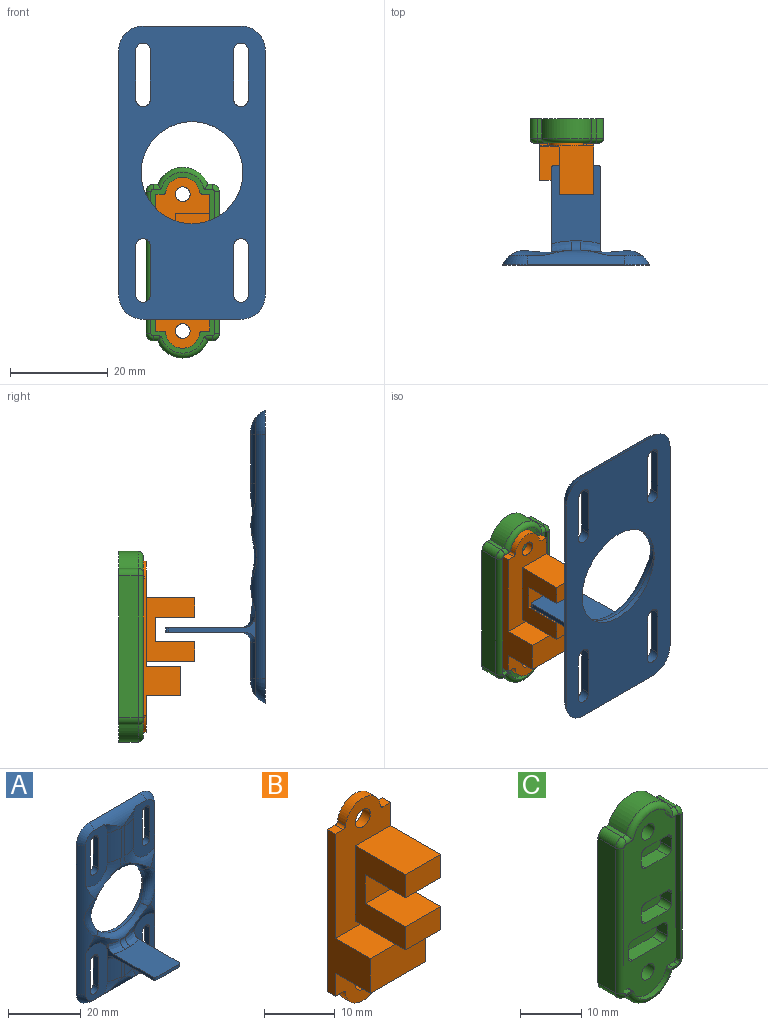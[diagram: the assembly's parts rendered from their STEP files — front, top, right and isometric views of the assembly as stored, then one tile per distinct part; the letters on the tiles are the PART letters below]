
ASSEMBLY  parts=3 mates=2
PART A: 62 faces, bbox 33.1x21.1x63.1 mm
  f0: plane 7.92x1.3mm, normal (0,-1,0), area 10.2mm2, adj f20,f42,f43,f44,f45,f58
  f1: plane 13.04x2.03mm, normal (0,-1,0), area 17.3mm2, adj f23,f36,f46,f47,f48,f49,f50,f51
  f2: cylinder r=1.5mm len=3mm, axis (0,1,0), area 9.4mm2, adj f3,f14,f27,f29
  f3: plane 10x2mm, normal (-1,0,0), area 20mm2, adj f2,f4,f27,f29
  f4: cylinder r=1.5mm len=3mm, axis (0,1,0), area 9.4mm2, adj f3,f14,f27,f29
  f5: cylinder r=1.5mm len=3mm, axis (0,1,0), area 9.4mm2, adj f6,f15,f27,f32
  f6: plane 10x2mm, normal (-1,0,0), area 20mm2, adj f5,f7,f27,f32
  f7: cylinder r=1.5mm len=3mm, axis (0,1,0), area 9.4mm2, adj f6,f15,f27,f32
  f8: cylinder r=1.5mm len=3mm, axis (0,1,0), area 9.4mm2, adj f9,f16,f27,f31
  f9: plane 10x2mm, normal (-1,0,0), area 20mm2, adj f8,f10,f27,f31
  f10: cylinder r=1.5mm len=3mm, axis (0,1,0), area 9.4mm2, adj f9,f16,f27,f31
  f11: cylinder r=1.5mm len=3mm, axis (0,1,0), area 9.4mm2, adj f12,f17,f27,f28
  f12: plane 10x2mm, normal (-1,0,0), area 20mm2, adj f11,f13,f27,f28
  f13: cylinder r=1.5mm len=3mm, axis (0,1,0), area 9.4mm2, adj f12,f17,f27,f28
  f14: plane 10x2mm, normal (1,0,0), area 20mm2, adj f2,f4,f27,f29
  f15: plane 10x2mm, normal (1,0,0), area 20mm2, adj f5,f7,f27,f32
  f16: plane 10x2mm, normal (1,0,0), area 20mm2, adj f8,f10,f27,f31
  f17: plane 10x2mm, normal (1,0,0), area 20mm2, adj f11,f13,f27,f28
  f18: torus R=0.42mm, axis (0,1,0), area 17.4mm2, adj f19,f20,f27,f32
  f19: cylinder r=5mm len=50mm, axis (0,0,-1), area 151.3mm2, adj f18,f21,f27,f31,f32,f35,f46,f53
  f20: cylinder r=5mm len=20mm, axis (-1,0,0), area 74.1mm2, adj f0,f18,f22,f27,f29,f32,f43,f45
  f21: torus R=0.42mm, axis (0,1,0), area 17.4mm2, adj f19,f23,f27,f31
  f22: torus R=0.42mm, axis (0,1,0), area 17.4mm2, adj f20,f24,f27,f29
  f23: cylinder r=5mm len=20mm, axis (-1,0,0), area 74.1mm2, adj f1,f21,f25,f27,f28,f31,f48,f51
  f24: cylinder r=5mm len=50mm, axis (0,0,-1), area 151.3mm2, adj f22,f25,f27,f28,f29,f38,f49,f52
  f25: torus R=0.42mm, axis (0,1,0), area 17.4mm2, adj f23,f24,f27,f28
  f26: plane 2.03x0.12mm, normal (0,-1,0), area 0.2mm2, adj f37,f52,f53,f55
  f27: plane 60x30mm, normal (0,1,0), area 1289.3mm2, adj f2,f3,f4,f5,f6,f7,f8,f9
  f28: plane 18.42x8.42mm, normal (0,-1,0), area 107.2mm2, adj f11,f12,f13,f17,f23,f24,f25,f49
  f29: plane 18.42x8.42mm, normal (0,-1,0), area 107.2mm2, adj f2,f3,f4,f14,f20,f22,f24,f30
  f30: plane 18.22x5.68mm, normal (-1,0,0), area 20.1mm2, adj f29,f39,f40,f52,f54,f57,f61
  f31: plane 18.42x8.42mm, normal (0,-1,0), area 107.2mm2, adj f8,f9,f10,f16,f19,f21,f23,f46
  f32: plane 18.42x8.42mm, normal (0,-1,0), area 107.2mm2, adj f5,f6,f7,f15,f18,f19,f20,f33
  f33: plane 18.22x5.68mm, normal (1,0,0), area 20.1mm2, adj f32,f39,f40,f53,f56,f59,f60
  f34: cylinder r=10.42mm len=20.84mm, axis (0,-1,0), area 56.1mm2, adj f27,f35,f36,f37,f38
  f35: bspline ~14.5x5.46mm, area 53.4mm2, adj f19,f34,f36,f37,f46,f53
  f36: torus R=12.42mm, axis (0,-1,0), area 51.2mm2, adj f1,f34,f35,f38,f46,f49
  f37: torus R=12.42mm, axis (0,-1,0), area 51.2mm2, adj f26,f34,f35,f38,f52,f53
  f38: bspline ~14.5x5.46mm, area 53.4mm2, adj f24,f34,f36,f37,f49,f52
  f39: plane 16.22x10mm, normal (0,0,-1), area 156.2mm2, adj f30,f33,f41,f57,f58,f59,f60,f61
  f40: plane 16.01x10mm, normal (0,0,1), area 155.5mm2, adj f30,f33,f41,f54,f55,f56,f60,f61
  f41: plane 9x1mm, normal (0,-1,0), area 9mm2, adj f39,f40,f60,f61
  f42: cylinder r=10mm len=7.5mm, axis (0,0,1), area 33.8mm2, adj f0,f29,f43,f57
  f43: torus R=9.36mm, axis (0,-1,0), area 9.2mm2, adj f0,f20,f29,f42
  f44: cylinder r=10mm len=7.5mm, axis (0,0,1), area 33.8mm2, adj f0,f32,f45,f59
  f45: torus R=9.36mm, axis (0,-1,0), area 9.2mm2, adj f0,f20,f32,f44
  f46: torus R=9.36mm, axis (0,-1,0), area 38.1mm2, adj f1,f19,f31,f35,f36,f47
  f47: cylinder r=10mm len=10mm, axis (0,0,1), area 45.1mm2, adj f1,f31,f46,f48
  f48: torus R=9.36mm, axis (0,-1,0), area 9.2mm2, adj f1,f23,f31,f47
  f49: torus R=9.36mm, axis (0,-1,0), area 38.1mm2, adj f1,f24,f28,f36,f38,f50
  f50: cylinder r=10mm len=10mm, axis (0,0,1), area 45.1mm2, adj f1,f28,f49,f51
  f51: torus R=9.36mm, axis (0,-1,0), area 9.2mm2, adj f1,f23,f28,f50
  f52: torus R=9.36mm, axis (0,-1,0), area 26.5mm2, adj f24,f26,f29,f30,f37,f38,f54
  f53: torus R=9.36mm, axis (0,-1,0), area 26.5mm2, adj f19,f26,f32,f33,f35,f37,f56
  f54: bspline ~5.71x3.34mm, area 13.1mm2, adj f30,f40,f52,f55
  f55: cylinder r=2mm len=2mm, axis (-1,0,0), area 6.2mm2, adj f26,f40,f54,f56
  f56: bspline ~5.71x3.34mm, area 13.1mm2, adj f33,f40,f53,f55
  f57: torus R=12mm, axis (0,0,-1), area 13.8mm2, adj f30,f39,f42,f58
  f58: cylinder r=2mm len=2mm, axis (1,0,0), area 4mm2, adj f0,f39,f57,f59
  f59: torus R=12mm, axis (0,0,-1), area 13.8mm2, adj f33,f39,f44,f58
  f60: cylinder r=0.5mm len=1mm, axis (0,0,1), area 0.8mm2, adj f33,f39,f40,f41
  f61: cylinder r=0.5mm len=1mm, axis (0,0,-1), area 0.8mm2, adj f30,f39,f40,f41
PART B: 28 faces, bbox 11x11.6x35 mm
  f0: plane 7x4mm, normal (0,-1,0), area 28mm2, adj f1,f22,f23,f26
  f1: plane 28x11.6mm, normal (1,0,0), area 176.8mm2, adj f0,f2,f3,f13,f14,f15,f18,f19
  f2: plane 21.5x11mm, normal (0,-1,0), area 119.3mm2, adj f1,f4,f5,f6,f7,f8,f14,f17
  f3: plane 11x7.5mm, normal (0,-1,0), area 56.3mm2, adj f1,f8,f9,f10,f11,f12,f13,f16
  f4: cylinder r=0.5mm len=1.6mm, axis (0,1,0), area 1.2mm2, adj f2,f5,f14,f15
  f5: cylinder r=3.5mm len=6.95mm, axis (0,1,0), area 16.2mm2, adj f2,f4,f6,f15
  f6: cylinder r=0.5mm len=1.6mm, axis (0,1,0), area 1.2mm2, adj f2,f5,f7,f15
  f7: plane 1.6x1.53mm, normal (0,0,1), area 2.5mm2, adj f2,f6,f8,f15
  f8: plane 28x8.6mm, normal (-1,0,0), area 86.8mm2, adj f2,f3,f7,f9,f15,f18,f19,f20
  f9: plane 1.6x1.53mm, normal (0,0,-1), area 2.5mm2, adj f3,f8,f10,f15
  f10: cylinder r=0.5mm len=1.6mm, axis (0,1,0), area 1.2mm2, adj f3,f9,f11,f15
  f11: cylinder r=3.5mm len=6.95mm, axis (0,1,0), area 16.2mm2, adj f3,f10,f12,f15
  f12: cylinder r=0.5mm len=1.6mm, axis (0,1,0), area 1.2mm2, adj f3,f11,f13,f15
  f13: plane 1.6x1.53mm, normal (0,0,-1), area 2.5mm2, adj f1,f3,f12,f15
  f14: plane 1.6x1.53mm, normal (0,0,1), area 2.5mm2, adj f1,f2,f4,f15
  f15: plane 35x11mm, normal (0,1,0), area 332.5mm2, adj f1,f4,f5,f6,f7,f8,f9,f10
  f16: cylinder r=1.5mm len=3mm, axis (0,1,0), area 15.1mm2, adj f3,f15
  f17: cylinder r=1.5mm len=3mm, axis (0,1,0), area 15.1mm2, adj f2,f15
  f18: plane 11x7mm, normal (0,0,1), area 77mm2, adj f1,f2,f8,f20
  f19: plane 11x7mm, normal (0,0,-1), area 77mm2, adj f1,f3,f8,f20
  f20: plane 11x6mm, normal (0,-1,0), area 66mm2, adj f1,f8,f18,f19
  f21: plane 10x7mm, normal (0,0,1), area 70mm2, adj f1,f2,f22,f24
  f22: plane 13x10mm, normal (-1,0,0), area 90mm2, adj f0,f2,f21,f23,f24,f25,f26,f27
  f23: plane 10x7mm, normal (0,0,-1), area 70mm2, adj f0,f1,f2,f22
  f24: plane 7x4mm, normal (0,-1,0), area 28mm2, adj f1,f21,f22,f25
  f25: plane 8x7mm, normal (0,0,-1), area 56mm2, adj f1,f22,f24,f27
  f26: plane 8x7mm, normal (0,0,1), area 56mm2, adj f0,f1,f22,f27
  f27: plane 7x5mm, normal (0,-1,0), area 35mm2, adj f1,f22,f25,f26
PART C: 71 faces, bbox 15x5x39.9 mm
  f0: plane 37x13mm, normal (0,-1,0), area 332.1mm2, adj f2,f3,f4,f5,f6,f7,f8,f9
  f1: plane 39x15mm, normal (0,1,0), area 516mm2, adj f10,f11,f12,f13,f14,f15,f16,f17
  f2: plane 29x1mm, normal (-1,0,0), area 29mm2, adj f0,f4,f5,f34
  f3: plane 29x1mm, normal (1,0,0), area 29mm2, adj f0,f7,f8,f37
  f4: cylinder r=0.5mm len=1mm, axis (0,1,0), area 0.8mm2, adj f0,f2,f28,f36
  f5: cylinder r=0.5mm len=1mm, axis (0,1,0), area 0.8mm2, adj f0,f2,f21,f32
  f6: cylinder r=4.5mm len=8.59mm, axis (0,1,0), area 11.4mm2, adj f0,f22,f23,f31
  f7: cylinder r=0.5mm len=1mm, axis (0,1,0), area 0.8mm2, adj f0,f3,f24,f35
  f8: cylinder r=0.5mm len=1mm, axis (0,1,0), area 0.8mm2, adj f0,f3,f25,f39
  f9: cylinder r=4.5mm len=8.59mm, axis (0,1,0), area 11.4mm2, adj f0,f26,f27,f40
  f10: cylinder r=5.5mm len=10.25mm, axis (0,1,0), area 52.7mm2, adj f1,f11,f29,f31
  f11: plane 4x0.88mm, normal (0,0,-1), area 3.5mm2, adj f1,f10,f12,f30
  f12: cylinder r=1.5mm len=4mm, axis (0,1,0), area 9.4mm2, adj f1,f11,f13,f32
  f13: plane 29x4mm, normal (1,0,0), area 116mm2, adj f1,f12,f14,f34
  f14: cylinder r=1.5mm len=4mm, axis (0,1,0), area 9.4mm2, adj f1,f13,f15,f36
  f15: plane 4x0.88mm, normal (0,0,1), area 3.5mm2, adj f1,f14,f16,f38
  f16: cylinder r=5.5mm len=10.25mm, axis (0,1,0), area 52.7mm2, adj f1,f15,f17,f40
  f17: plane 4x0.88mm, normal (0,0,1), area 3.5mm2, adj f1,f16,f18,f41
  f18: cylinder r=1.5mm len=4mm, axis (0,1,0), area 9.4mm2, adj f1,f17,f19,f39
  f19: plane 29x4mm, normal (-1,0,0), area 116mm2, adj f1,f18,f20,f37
  f20: cylinder r=1.5mm len=4mm, axis (0,1,0), area 9.4mm2, adj f1,f19,f29,f35
  f21: plane 1.23x1mm, normal (0,0,1), area 1.2mm2, adj f0,f5,f22,f30
  f22: cylinder r=0.5mm len=1mm, axis (0,1,0), area 0.6mm2, adj f0,f6,f21,f30,f31
  f23: cylinder r=0.5mm len=1mm, axis (0,1,0), area 0.6mm2, adj f0,f6,f24,f31,f33
  f24: plane 1.23x1mm, normal (0,0,1), area 1.2mm2, adj f0,f7,f23,f33
  f25: plane 1.23x1mm, normal (0,0,-1), area 1.2mm2, adj f0,f8,f26,f41
  f26: cylinder r=0.5mm len=1mm, axis (0,1,0), area 0.6mm2, adj f0,f9,f25,f40,f41
  f27: cylinder r=0.5mm len=1mm, axis (0,1,0), area 0.6mm2, adj f0,f9,f28,f38,f40
  f28: plane 1.23x1mm, normal (0,0,-1), area 1.2mm2, adj f0,f4,f27,f38
  f29: plane 4x0.88mm, normal (0,0,-1), area 3.5mm2, adj f1,f10,f20,f33
  f30: cylinder r=1mm len=1.53mm, axis (-1,0,0), area 1.8mm2, adj f11,f21,f22,f31,f32
  f31: torus R=4.5mm, axis (0,-1,0), area 20.1mm2, adj f6,f10,f22,f23,f30,f33
  f32: torus R=0.5mm, axis (0,-1,0), area 2.8mm2, adj f5,f12,f30,f34
  f33: cylinder r=1mm len=1.53mm, axis (-1,0,0), area 1.8mm2, adj f23,f24,f29,f31,f35
  f34: cylinder r=1mm len=29mm, axis (0,0,-1), area 45.6mm2, adj f2,f13,f32,f36
  f35: torus R=0.5mm, axis (0,-1,0), area 2.8mm2, adj f7,f20,f33,f37
  f36: torus R=0.5mm, axis (0,-1,0), area 2.8mm2, adj f4,f14,f34,f38
  f37: cylinder r=1mm len=29mm, axis (0,0,1), area 45.6mm2, adj f3,f19,f35,f39
  f38: cylinder r=1mm len=1.53mm, axis (1,0,0), area 1.8mm2, adj f15,f27,f28,f36,f40
  f39: torus R=0.5mm, axis (0,-1,0), area 2.8mm2, adj f8,f18,f37,f41
  f40: torus R=4.5mm, axis (0,-1,0), area 20.1mm2, adj f9,f16,f26,f27,f38,f41
  f41: cylinder r=1mm len=1.53mm, axis (1,0,0), area 1.8mm2, adj f17,f25,f26,f39,f40
  f42: cylinder r=1.5mm len=4mm, axis (0,1,0), area 37.7mm2, adj f0,f1
  f43: cylinder r=1.5mm len=4mm, axis (0,1,0), area 37.7mm2, adj f0,f1
  f44: plane 5x2.5mm, normal (0,0,1), area 12.5mm2, adj f0,f45,f51,f52
  f45: cylinder r=1mm len=2.5mm, axis (0,-1,0), area 3.9mm2, adj f0,f44,f46,f52
  f46: plane 2.5x2mm, normal (-1,0,0), area 5mm2, adj f0,f45,f47,f52
  f47: cylinder r=1mm len=2.5mm, axis (0,-1,0), area 3.9mm2, adj f0,f46,f48,f52
  f48: plane 5x2.5mm, normal (0,0,-1), area 12.5mm2, adj f0,f47,f49,f52
  f49: cylinder r=1mm len=2.5mm, axis (0,-1,0), area 3.9mm2, adj f0,f48,f50,f52
  f50: plane 2.5x2mm, normal (1,0,0), area 5mm2, adj f0,f49,f51,f52
  f51: cylinder r=1mm len=2.5mm, axis (0,-1,0), area 3.9mm2, adj f0,f44,f50,f52
  f52: plane 7x4mm, normal (0,-1,0), area 27.1mm2, adj f44,f45,f46,f47,f48,f49,f50,f51
  f53: plane 5x2.5mm, normal (0,0,1), area 12.5mm2, adj f0,f54,f60,f61
  f54: cylinder r=1mm len=2.5mm, axis (0,-1,0), area 3.9mm2, adj f0,f53,f55,f61
  f55: plane 2.5x2mm, normal (-1,0,0), area 5mm2, adj f0,f54,f56,f61
  f56: cylinder r=1mm len=2.5mm, axis (0,-1,0), area 3.9mm2, adj f0,f55,f57,f61
  f57: plane 5x2.5mm, normal (0,0,-1), area 12.5mm2, adj f0,f56,f58,f61
  f58: cylinder r=1mm len=2.5mm, axis (0,-1,0), area 3.9mm2, adj f0,f57,f59,f61
  f59: plane 2.5x2mm, normal (1,0,0), area 5mm2, adj f0,f58,f60,f61
  f60: cylinder r=1mm len=2.5mm, axis (0,-1,0), area 3.9mm2, adj f0,f53,f59,f61
  f61: plane 7x4mm, normal (0,-1,0), area 27.1mm2, adj f53,f54,f55,f56,f57,f58,f59,f60
  f62: plane 7x2.5mm, normal (0,0,-1), area 17.5mm2, adj f0,f63,f69,f70
  f63: cylinder r=1mm len=2.5mm, axis (0,-1,0), area 3.9mm2, adj f0,f62,f64,f70
  f64: plane 2.5x2mm, normal (1,0,0), area 5mm2, adj f0,f63,f65,f70
  f65: cylinder r=1mm len=2.5mm, axis (0,-1,0), area 3.9mm2, adj f0,f64,f66,f70
  f66: plane 7x2.5mm, normal (0,0,1), area 17.5mm2, adj f0,f65,f67,f70
  f67: cylinder r=1mm len=2.5mm, axis (0,-1,0), area 3.9mm2, adj f0,f66,f68,f70
  f68: plane 2.5x2mm, normal (-1,0,0), area 5mm2, adj f0,f67,f69,f70
  f69: cylinder r=1mm len=2.5mm, axis (0,-1,0), area 3.9mm2, adj f0,f62,f68,f70
  f70: plane 9x4mm, normal (0,-1,0), area 35.1mm2, adj f62,f63,f64,f65,f66,f67,f68,f69
PLACE A rot(axis=(0,0,1),180deg) t=(1.89,-30,3.41)mm
PLACE B t=(0,-4,0)mm
PLACE C at identity fixed
MATE fastened C.f9 <-> B.f5  axis (0,-1,0) through (0,-4,14)mm
MATE parallel C.f1 <-> A.f34  axis (0,1,0) through (0,0,0)mm
